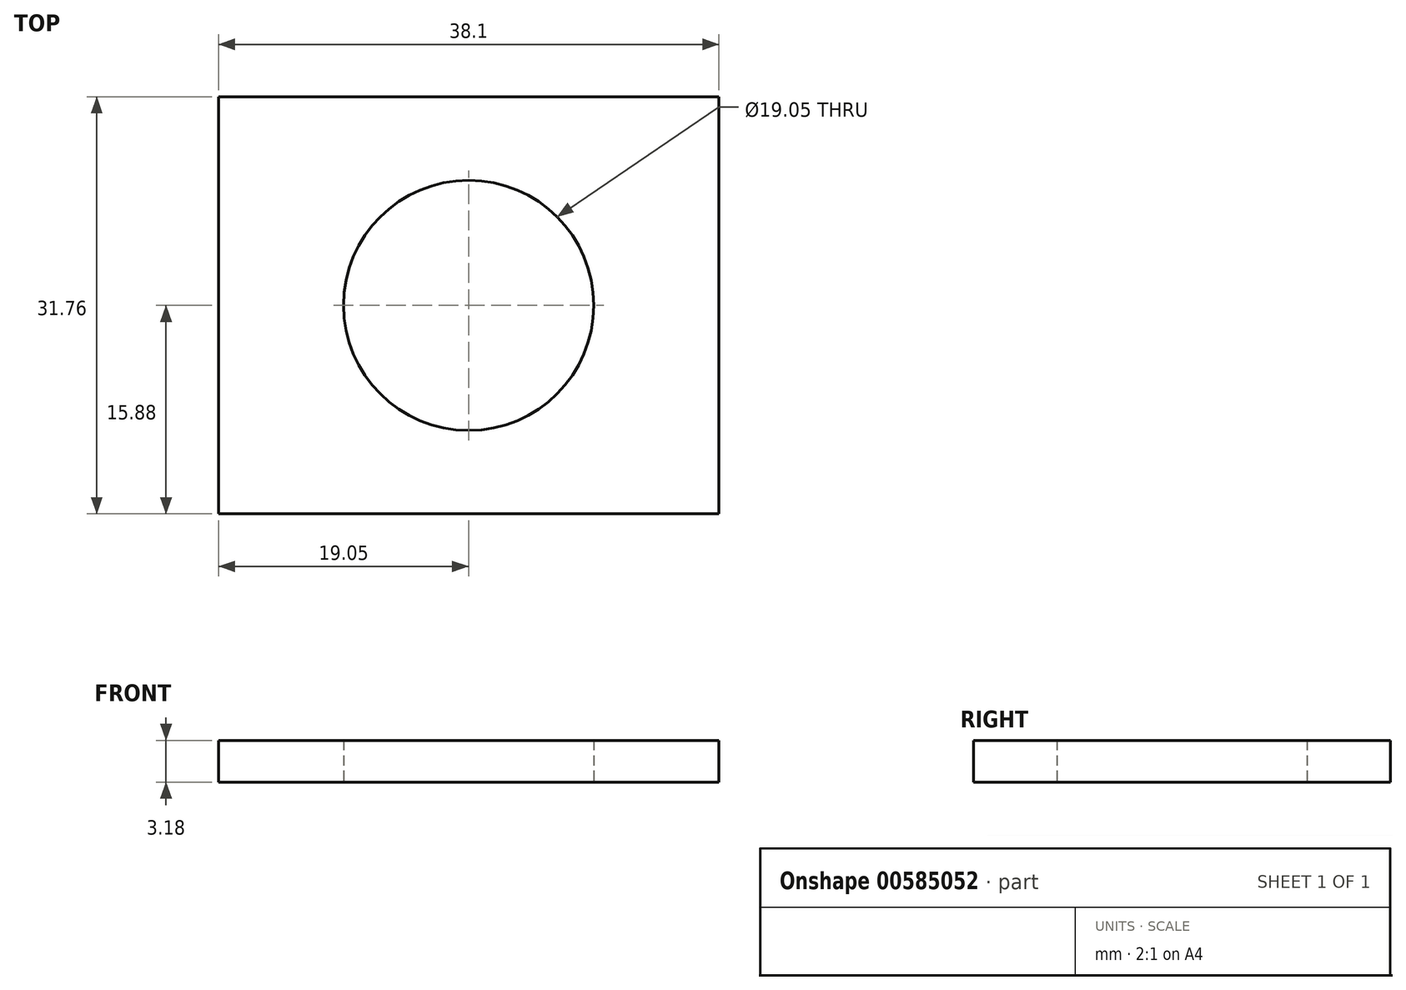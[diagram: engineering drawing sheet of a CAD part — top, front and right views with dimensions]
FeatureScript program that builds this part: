
annotation { "Feature Type Name" : "Feature", "Feature Type Description" : "" }
export const myFeature = defineFeature(function(context is Context, id is Id, definition is map)
    precondition{}
    {
        {
            var Q0;
            Q0=qCreatedBy(makeId("Top.planeOp"),FACE);
            var sketch = newSketch(context, id + "F0", { "sketchPlane" : qUnion([Q0])});
            skCircle(sketch, "E0", {"center": v(0, 0) * mm, "radius": 9.53 * mm});
            skLineSegment(sketch, "E1.bottom", {"start": v(19.05, 15.88) * mm, "end": v(-19.05, 15.88) * mm});
            skLineSegment(sketch, "E1.top", {"start": v(19.05, -15.88) * mm, "end": v(-19.05, -15.88) * mm});
            skLineSegment(sketch, "E1.left", {"start": v(19.05, 15.88) * mm, "end": v(19.05, -15.88) * mm});
            skLineSegment(sketch, "E1.right", {"start": v(-19.05, 15.88) * mm, "end": v(-19.05, -15.88) * mm});
            skSolve(sketch);
        }
        {
            var Q0;
            Q0 = qSketchRegion(id + "F0", true);
            extrude(context, id + "F1", {"entities" : qUnion([Q0]), "depth" : 3.17 * mm, "offsetDistance" : 25.4 * mm});
        }
    });
